# Revit family: 800.440 2C
name_source: partatom
category: Plumbing Fixtures
revit_build: Autodesk Revit 2017 (Build: 20160225_1515(x64)
units: mm (PartAtom-declared; Revit-internal decimal feet)

## family parameters
Cut with Voids When Loaded = Yes
Host = Face
Part Type = Normal
Room Calculation Point = No
Round Connector Dimension = Use Diameter
Shared = No

## types (1)
- 800.440 2C
    Acabado_Lavaplatos = Teka_Acero Inoxidable
    Ancho = 800 mm  [stored 2.62467 ft]
    Ancho encastre = 420 mm
    Ca_1_Accesorios = Válvula 1 1/2'' + Rebalse redondo
    Ca_1_Dimensiones Lavaplatos = 800 x 440 mm
    Ca_1_Dimesiones Cubeta = 370 x 340 x 138 mm
    Ca_1_Espesor de acero = 0,7 mm
    Ca_1_Instalación = Empotrado
    Ca_1_Material Principal = Acero Inoxidable AISI-304 (18/10)
    Ca_1_Profundidad Cubeta = 138 mm
    Ca_1_Sello CE = Producto cumple Norma Europea EN-13310
    Ca_Certificaciones = Norma Europea EN-13310
    Ca_Creado por = Catálogo Arquitectura
    Ca_Código Catálogo Arquitectura = 411_TEK_051
    Ca_Código EAN = 8421152016114
    Ca_Código del Producto = 10103011
    Ca_Especificaciones Técnicas = Lavaplatos empotrable de acero TEKA modelo 800.440 2C
    Ca_Fabricante = Teka
    Ca_Instalación = Empotrable
    Ca_Itemizado CDT = E 04 05 09
    Ca_Masterformat = 22 41 16
    Ca_Material Principal = Acero Inoxidable AISI-304 (18/10)
    Ca_País de Fabricación = España
    Ca_Producto = Lavaplatos Empotrable Teka Modelo 800.440 2C
    Ca_Profundidad = 138 mm  [stored 0.452756 ft]
    Ca_Representante = Teka
    Ca_Teléfono = 99821 1017
    Ca_Usos = Lavaplatos empotrable para cocina
    Ca_Web del Fabricante = www.teka.cl
    Ca_Web del Representante = www.teka.cl
    Default Elevation = 1219.2 mm  [stored 4 ft]
    Description = Lavaplatos empotrable para cocina
    Encastre lavaplato = 780 mm
    Fondo = 440 mm  [stored 1.44357 ft]
    Manufacturer = Teka
    Model = 800.440 2C
    URL = www.teka.cl
    Waste Connection = Yes

note: [stored X ft] marks values corroborated as IEEE doubles in the binary element streams (Revit-internal decimal feet)

## geometry (parser evidence)
native form markers: Sweep x3
no freeform markers — native parametric forms only
